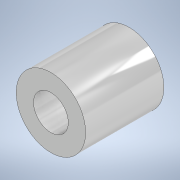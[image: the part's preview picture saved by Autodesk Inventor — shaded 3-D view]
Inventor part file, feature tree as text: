
AUTODESK INVENTOR PART (.ipt)
format: ipt  version: 2021 (Build 250183000, 183)  size: 103,936 bytes
history: native  units: mm
features: extrude x2, sketch x2
ambient origin geometry x8: Origin, YZ Plane, XZ Plane, XY Plane, X Axis, Y Axis, Z Axis, Center Point
bodies: Solid1 (feature_tree)
feature tree (4):
  extrude  "Extrusion1"  Depth=6.75mm TaperAngle=0.0deg
  extrude  "Extrusion2"  TaperAngle=0.0deg  [1 undecoded]
  sketch  "Sketch1"  dims[d0=6.0mm d1=6.75mm d2=0.0mm]
  sketch  "Sketch2"  dims[d3=3.0mm d4=0.0mm d5=0.0mm]
note: 1 required parameter value undecoded (feature->parameter linkage not recoverable at this tier; creation-order binding heuristic only, values carry confidence <= 0.55)
